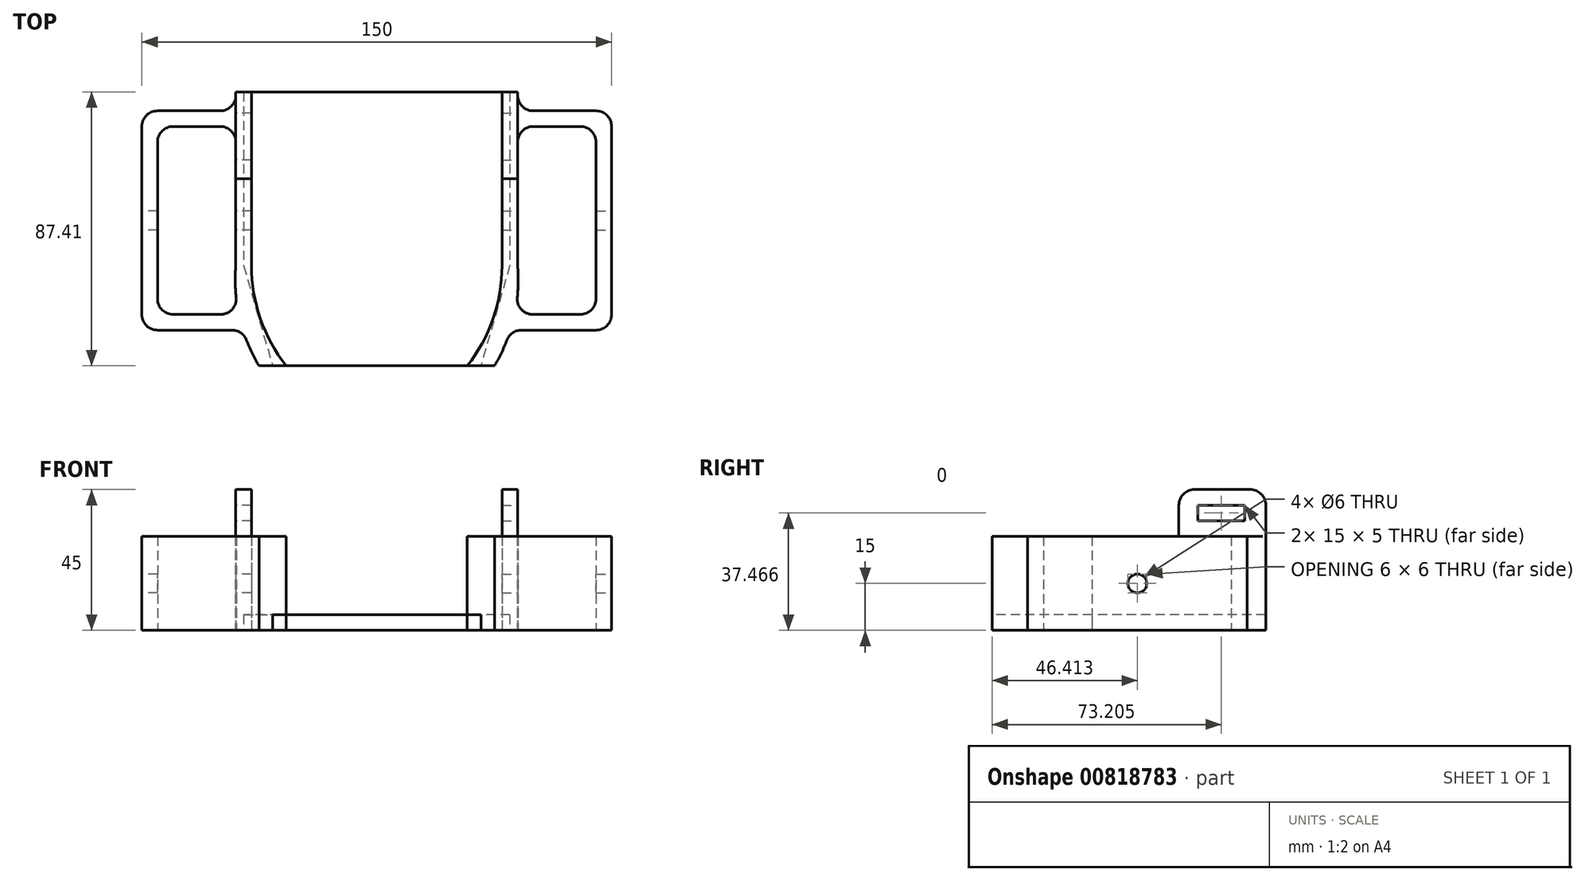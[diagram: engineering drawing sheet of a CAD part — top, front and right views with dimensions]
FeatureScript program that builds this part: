
annotation { "Feature Type Name" : "Feature", "Feature Type Description" : "" }
export const myFeature = defineFeature(function(context is Context, id is Id, definition is map)
    precondition{}
    {
        {
            var Q0;
            Q0=qCreatedBy(makeId("Top.planeOp"),FACE);
            var sketch = newSketch(context, id + "F0", { "sketchPlane" : qUnion([Q0])});
            skArc(sketch, "E0", {"start": v(-45, 0) * mm, "mid": v(-43.78, -16.56) * mm, "end": v(-37.6, -31.97) * mm});
            skLineSegment(sketch, "E1", {"start": v(-45, 0) * mm, "end": v(-45, 55.44) * mm});
            skLineSegment(sketch, "E2", {"start": v(-45, 49.44) * mm, "end": v(-75, 49.44) * mm});
            skLineSegment(sketch, "E3", {"start": v(-75, 49.44) * mm, "end": v(-75, -20.56) * mm});
            skLineSegment(sketch, "E4", {"start": v(-75, -20.56) * mm, "end": v(-42.7, -20.56) * mm});
            skLineSegment(sketch, "E5", {"start": v(-45, 44.44) * mm, "end": v(-70, 44.44) * mm});
            skLineSegment(sketch, "E6", {"start": v(-70, 44.44) * mm, "end": v(-70, -15.56) * mm});
            skLineSegment(sketch, "E7", {"start": v(-70, -15.56) * mm, "end": v(-44, -15.56) * mm});
            skLineSegment(sketch, "E8.MirrorCS", {"start": v(45, 0) * mm, "end": v(45, 55.44) * mm});
            skArc(sketch, "E9.MirrorCS", {"start": v(45, 0) * mm, "mid": v(43.78, -16.56) * mm, "end": v(37.6, -31.97) * mm});
            skLineSegment(sketch, "E10.MirrorCS", {"start": v(70, -15.56) * mm, "end": v(44, -15.56) * mm});
            skLineSegment(sketch, "E11.MirrorCS", {"start": v(75, -20.56) * mm, "end": v(42.7, -20.56) * mm});
            skLineSegment(sketch, "E12.MirrorCS", {"start": v(75, 49.44) * mm, "end": v(75, -20.56) * mm});
            skLineSegment(sketch, "E13.MirrorCS", {"start": v(70, 44.44) * mm, "end": v(70, -15.56) * mm});
            skLineSegment(sketch, "E14.MirrorCS", {"start": v(45, 44.44) * mm, "end": v(70, 44.44) * mm});
            skLineSegment(sketch, "E15.MirrorCS", {"start": v(45, 49.44) * mm, "end": v(75, 49.44) * mm});
            skLineSegment(sketch, "E16", {"start": v(-40, 55.44) * mm, "end": v(-40, 0) * mm});
            skArc(sketch, "E17", {"start": v(-40, 0) * mm, "mid": v(-37.14, -16.92) * mm, "end": v(-28.89, -31.97) * mm});
            skLineSegment(sketch, "E18.MirrorCS", {"start": v(40, 55.44) * mm, "end": v(40, 0) * mm});
            skArc(sketch, "E19.MirrorCS", {"start": v(40, 0) * mm, "mid": v(37.14, -16.92) * mm, "end": v(28.89, -31.97) * mm});
            skLineSegment(sketch, "E20", {"start": v(-45, 55.44) * mm, "end": v(-40, 55.44) * mm});
            skLineSegment(sketch, "E21.MirrorCS", {"start": v(45, 55.44) * mm, "end": v(40, 55.44) * mm});
            skLineSegment(sketch, "E22", {"start": v(-37.6, -31.97) * mm, "end": v(-28.89, -31.97) * mm});
            skPoint(sketch, "E23.orphan", {"position": v(0, -57.67) * mm});
            skLineSegment(sketch, "E24.trimOffspring", {"start": v(28.89, -31.97) * mm, "end": v(37.6, -31.97) * mm});
            skPoint(sketch, "E25.orphan", {"position": v(0, -50.23) * mm});
            skSolve(sketch);
        }
        {
            var Q0;
            Q0=qSketchRegion(id+"F0",true);
            extrude(context, id + "F1", {"entities" : qUnion([Q0]), "depth" : 30 * mm, "offsetDistance" : 25 * mm});
        }
        {
            var Q0;
            Q0=makeQuery(id+"F1.opExtrude","CAP_FACE",FACE,{"disambiguationData":[OSD([sQuery(id+"F0.wireOp",EDGE,"E0"),sQuery(id+"F0.wireOp",EDGE,"E1"),sQuery(id+"F0.wireOp",EDGE,"E2"),sQuery(id+"F0.wireOp",EDGE,"E3"),sQuery(id+"F0.wireOp",EDGE,"E4"),sQuery(id+"F0.wireOp",EDGE,"E5"),sQuery(id+"F0.wireOp",EDGE,"E6"),sQuery(id+"F0.wireOp",EDGE,"E7"),sQuery(id+"F0.wireOp",EDGE,"E16"),sQuery(id+"F0.wireOp",EDGE,"E17"),sQuery(id+"F0.wireOp",EDGE,"E20"),sQuery(id+"F0.wireOp",EDGE,"E22")])],"isStart":true});
            var sketch = newSketch(context, id + "F2", { "sketchPlane" : qUnion([Q0])});
            skLineSegment(sketch, "E26", {"start": v(-42.5, -55.44) * mm, "end": v(0, -55.44) * mm});
            skLineSegment(sketch, "E27", {"start": v(0, -55.44) * mm, "end": v(0, 31.97) * mm});
            skLineSegment(sketch, "E28", {"start": v(0, 31.97) * mm, "end": v(-33.24, 31.97) * mm});
            skLineSegment(sketch, "E29.MirrorCS", {"start": v(42.5, -55.44) * mm, "end": v(0, -55.44) * mm});
            skLineSegment(sketch, "E30.MirrorCS", {"start": v(0, 31.97) * mm, "end": v(33.24, 31.97) * mm});
            skLineSegment(sketch, "E31", {"start": v(-42.5, -55.44) * mm, "end": v(-42.5, 0) * mm});
            skLineSegment(sketch, "E32", {"start": v(-42.5, 0) * mm, "end": v(-33.24, 31.97) * mm});
            skLineSegment(sketch, "E33.MirrorCS", {"start": v(42.5, -55.44) * mm, "end": v(42.5, 0) * mm});
            skLineSegment(sketch, "E34.MirrorCS", {"start": v(42.5, 0) * mm, "end": v(33.24, 31.97) * mm});
            skSolve(sketch);
        }
        {
            var Q0;
            Q0=qSketchRegion(id+"F2",true);
            extrude(context, id + "F3", {"entities" : qUnion([Q0]), "oppositeDirection" : true, "depth" : 5 * mm, "offsetDistance" : 25 * mm});
        }
        {
            var Q0;
            Q0=makeQuery(id+"F1.opExtrude","SWEPT_FACE",FACE,{"disambiguationData":[OSD([sQuery(id+"F0.wireOp",EDGE,"E12.MirrorCS")])]});
            var sketch = newSketch(context, id + "F4", { "sketchPlane" : qUnion([Q0])});
            skCircle(sketch, "E35", {"center": v(14.44, 15) * mm, "radius": 3 * mm});
            skSolve(sketch);
        }
        {
            var Q0;
            Q0=qSketchRegion(id+"F4",true);
            extrude(context, id + "F5", {"entities" : qUnion([Q0]), "operationType" : NewBodyOperationType.REMOVE, "oppositeDirection" : true, "depth" : 35 * mm, "offsetDistance" : 25 * mm});
        }
        {
            var Q0;
            Q0=makeQuery(id+"F1.opExtrude","SWEPT_FACE",FACE,{"disambiguationData":[OSD([sQuery(id+"F0.wireOp",EDGE,"E3")])]});
            var sketch = newSketch(context, id + "F6", { "sketchPlane" : qUnion([Q0])});
            skCircle(sketch, "E36", {"center": v(-14.44, 15) * mm, "radius": 3 * mm});
            skSolve(sketch);
        }
        {
            var Q0;
            Q0=qSketchRegion(id+"F6",true);
            extrude(context, id + "F7", {"entities" : qUnion([Q0]), "operationType" : NewBodyOperationType.REMOVE, "oppositeDirection" : true, "depth" : 35 * mm, "offsetDistance" : 25 * mm});
        }
        {
            var Q0;
            Q0=makeQuery(id+"F1.opExtrude","SWEPT_FACE",FACE,{"disambiguationData":[OSD([sQuery(id+"F0.wireOp",EDGE,"E18.MirrorCS")])]});
            var sketch = newSketch(context, id + "F8", { "sketchPlane" : qUnion([Q0])});
            skPoint(sketch, "E37.oppositeSnap0", {"position": v(-27.72, 30) * mm});
            skLineSegment(sketch, "E37.bottom", {"start": v(-55.44, 30) * mm, "end": v(-27.72, 30) * mm});
            skLineSegment(sketch, "E37.top", {"start": v(-55.44, 45) * mm, "end": v(-27.72, 45) * mm});
            skLineSegment(sketch, "E37.left", {"start": v(-55.44, 30) * mm, "end": v(-55.44, 45) * mm});
            skLineSegment(sketch, "E37.right", {"start": v(-27.72, 30) * mm, "end": v(-27.72, 45) * mm});
            skLineSegment(sketch, "E38.bottom", {"start": v(-48.74, 39.97) * mm, "end": v(-33.74, 39.97) * mm});
            skLineSegment(sketch, "E38.top", {"start": v(-48.74, 34.97) * mm, "end": v(-33.74, 34.97) * mm});
            skLineSegment(sketch, "E38.left", {"start": v(-48.74, 39.97) * mm, "end": v(-48.74, 34.97) * mm});
            skLineSegment(sketch, "E38.right", {"start": v(-33.74, 39.97) * mm, "end": v(-33.74, 34.97) * mm});
            skSolve(sketch);
        }
        {
            var Q0;
            {var subQ0=sQuery(id+"F0.wireOp",EDGE,"E1");Q0=makeQuery(id+"F1.opExtrude","SWEPT_FACE",FACE,{"disambiguationData":[OSD([subQ0]),TDD([makeQuery(id+"F0.imprint","IMPRINT",EDGE,{"disambiguationData":[TD([[makeQuery(id+"F0.imprint","INTERSECT",VERTEX,{"derivedFrom":[subQ0,sQuery(id+"F0.wireOp",EDGE,"E20")]}),1.0]])],"derivedFrom":subQ0})])]});}
            var sketch = newSketch(context, id + "F9", { "sketchPlane" : qUnion([Q0])});
            skLineSegment(sketch, "E39.bottom", {"start": v(-55.44, 45) * mm, "end": v(-27.72, 45) * mm});
            skLineSegment(sketch, "E39.top", {"start": v(-55.44, 30) * mm, "end": v(-27.72, 30) * mm});
            skLineSegment(sketch, "E39.left", {"start": v(-55.44, 45) * mm, "end": v(-55.44, 30) * mm});
            skLineSegment(sketch, "E39.right", {"start": v(-27.72, 45) * mm, "end": v(-27.72, 30) * mm});
            skLineSegment(sketch, "E40.bottom", {"start": v(-48.74, 39.97) * mm, "end": v(-33.74, 39.97) * mm});
            skLineSegment(sketch, "E40.top", {"start": v(-48.74, 34.97) * mm, "end": v(-33.74, 34.97) * mm});
            skLineSegment(sketch, "E40.left", {"start": v(-48.74, 39.97) * mm, "end": v(-48.74, 34.97) * mm});
            skLineSegment(sketch, "E40.right", {"start": v(-33.74, 39.97) * mm, "end": v(-33.74, 34.97) * mm});
            skSolve(sketch);
        }
        {
            var Q0;
            Q0=qSketchRegion(id+"F9",true);
            extrude(context, id + "F10", {"entities" : qUnion([Q0]), "operationType" : NewBodyOperationType.ADD, "oppositeDirection" : true, "depth" : 5 * mm, "offsetDistance" : 25 * mm});
        }
        {
            var Q0;
            Q0=makeQuery(id+"F1.opExtrude","SWEPT_EDGE",EDGE,{"disambiguationData":[OSD([sQuery(id+"F0.wireOp",EDGE,"E2"),sQuery(id+"F0.wireOp",EDGE,"E3")])]});
            var Q1;
            Q1=makeQuery(id+"F1.opExtrude","SWEPT_EDGE",EDGE,{"disambiguationData":[OSD([sQuery(id+"F0.wireOp",EDGE,"E3"),sQuery(id+"F0.wireOp",EDGE,"E4")])]});
            fillet(context, id + "F11", {"entities" : qUnion([Q0, Q1]), "radius" : 5 * mm, "tangentPropagation" : true, "allowEdgeOverflow" : false});
        }
        {
            var Q0;
            Q0=makeQuery(id+"F1.opExtrude","SWEPT_EDGE",EDGE,{"disambiguationData":[OSD([sQuery(id+"F0.wireOp",EDGE,"E11.MirrorCS"),sQuery(id+"F0.wireOp",EDGE,"E12.MirrorCS")])]});
            var Q1;
            Q1=makeQuery(id+"F1.opExtrude","SWEPT_EDGE",EDGE,{"disambiguationData":[OSD([sQuery(id+"F0.wireOp",EDGE,"E12.MirrorCS"),sQuery(id+"F0.wireOp",EDGE,"E15.MirrorCS")])]});
            fillet(context, id + "F12", {"entities" : qUnion([Q0, Q1]), "radius" : 5 * mm, "tangentPropagation" : true, "allowEdgeOverflow" : false});
        }
        {
            var Q0;
            Q0=makeQuery(id+"F1.opExtrude","SWEPT_EDGE",EDGE,{"disambiguationData":[OSD([sQuery(id+"F0.wireOp",EDGE,"E13.MirrorCS"),sQuery(id+"F0.wireOp",EDGE,"E14.MirrorCS")])]});
            var Q1;
            Q1=makeQuery(id+"F1.opExtrude","SWEPT_EDGE",EDGE,{"disambiguationData":[OSD([sQuery(id+"F0.wireOp",EDGE,"E10.MirrorCS"),sQuery(id+"F0.wireOp",EDGE,"E13.MirrorCS")])]});
            var Q2;
            Q2=makeQuery(id+"F1.opExtrude","SWEPT_EDGE",EDGE,{"disambiguationData":[OSD([sQuery(id+"F0.wireOp",EDGE,"E5"),sQuery(id+"F0.wireOp",EDGE,"E6")])]});
            var Q3;
            Q3=makeQuery(id+"F1.opExtrude","SWEPT_EDGE",EDGE,{"disambiguationData":[OSD([sQuery(id+"F0.wireOp",EDGE,"E6"),sQuery(id+"F0.wireOp",EDGE,"E7")])]});
            var Q4;
            Q4=makeQuery(id+"F1.opExtrude","SWEPT_EDGE",EDGE,{"disambiguationData":[OSD([sQuery(id+"F0.wireOp",EDGE,"E1"),sQuery(id+"F0.wireOp",EDGE,"E5")])]});
            var Q5;
            Q5=makeQuery(id+"F1.opExtrude","SWEPT_EDGE",EDGE,{"disambiguationData":[OSD([sQuery(id+"F0.wireOp",EDGE,"E8.MirrorCS"),sQuery(id+"F0.wireOp",EDGE,"E14.MirrorCS")])]});
            var Q6;
            Q6=makeQuery(id+"F1.opExtrude","SWEPT_EDGE",EDGE,{"disambiguationData":[OSD([sQuery(id+"F0.wireOp",EDGE,"E9.MirrorCS"),sQuery(id+"F0.wireOp",EDGE,"E10.MirrorCS")])]});
            var Q7;
            Q7=makeQuery(id+"F1.opExtrude","SWEPT_EDGE",EDGE,{"disambiguationData":[OSD([sQuery(id+"F0.wireOp",EDGE,"E0"),sQuery(id+"F0.wireOp",EDGE,"E7")])]});
            var Q8;
            Q8=makeQuery(id+"F1.opExtrude","SWEPT_EDGE",EDGE,{"disambiguationData":[OSD([sQuery(id+"F0.wireOp",EDGE,"E9.MirrorCS"),sQuery(id+"F0.wireOp",EDGE,"E11.MirrorCS")])]});
            var Q9;
            Q9=makeQuery(id+"F1.opExtrude","SWEPT_EDGE",EDGE,{"disambiguationData":[OSD([sQuery(id+"F0.wireOp",EDGE,"E0"),sQuery(id+"F0.wireOp",EDGE,"E4")])]});
            var Q10;
            Q10=makeQuery(id+"F1.opExtrude","SWEPT_EDGE",EDGE,{"disambiguationData":[OSD([sQuery(id+"F0.wireOp",EDGE,"E8.MirrorCS"),sQuery(id+"F0.wireOp",EDGE,"E15.MirrorCS")])]});
            var Q11;
            Q11=makeQuery(id+"F1.opExtrude","SWEPT_EDGE",EDGE,{"disambiguationData":[OSD([sQuery(id+"F0.wireOp",EDGE,"E1"),sQuery(id+"F0.wireOp",EDGE,"E2")])]});
            var Q12;
            Q12=makeQuery(id+"F10.opExtrude","SWEPT_EDGE",EDGE,{"disambiguationData":[OSD([sQuery(id+"F9.wireOp",EDGE,"E39.top"),sQuery(id+"F9.wireOp",EDGE,"E39.right")])]});
            fillet(context, id + "F13", {"entities" : qUnion([Q0, Q1, Q2, Q3, Q4, Q5, Q6, Q7, Q8, Q9, Q10, Q11, Q12]), "radius" : 5 * mm, "tangentPropagation" : true, "allowEdgeOverflow" : false});
        }
        {
            var Q0;
            Q0=makeQuery(id+"F10.opExtrude","SWEPT_EDGE",EDGE,{"disambiguationData":[OSD([sQuery(id+"F9.wireOp",EDGE,"E39.bottom"),sQuery(id+"F9.wireOp",EDGE,"E39.left")])]});
            var Q1;
            Q1=makeQuery(id+"FJua1TxrDA2uPtG_3.opExtrude","SWEPT_EDGE",EDGE,{"disambiguationData":[OSD([sQuery(id+"F8.wireOp",EDGE,"E37.top"),sQuery(id+"F8.wireOp",EDGE,"E37.left")])]});
            var Q2;
            Q2=makeQuery(id+"FJua1TxrDA2uPtG_3.opExtrude","SWEPT_EDGE",EDGE,{"disambiguationData":[OSD([sQuery(id+"F8.wireOp",EDGE,"E37.top"),sQuery(id+"F8.wireOp",EDGE,"E37.right")])]});
            var Q3;
            Q3=makeQuery(id+"F10.opExtrude","SWEPT_EDGE",EDGE,{"disambiguationData":[OSD([sQuery(id+"F9.wireOp",EDGE,"E39.bottom"),sQuery(id+"F9.wireOp",EDGE,"E39.right")])]});
            fillet(context, id + "F14", {"entities" : qUnion([Q0, Q1, Q2, Q3]), "radius" : 5 * mm, "tangentPropagation" : true, "allowEdgeOverflow" : false});
        }
        {
            var Q0;
            {var subQ0=sQuery(id+"F0.wireOp",EDGE,"E8.MirrorCS");Q0=makeQuery(id+"F1.opExtrude","SWEPT_FACE",FACE,{"disambiguationData":[OSD([subQ0]),TDD([makeQuery(id+"F0.imprint","IMPRINT",EDGE,{"disambiguationData":[TD([[makeQuery(id+"F0.imprint","INTERSECT",VERTEX,{"derivedFrom":[subQ0,sQuery(id+"F0.wireOp",EDGE,"E9.MirrorCS")]}),-1.0]])],"derivedFrom":subQ0})])]});}
            var sketch = newSketch(context, id + "F15", { "sketchPlane" : qUnion([Q0])});
            skLineSegment(sketch, "E41.bottom", {"start": v(27.72, 45) * mm, "end": v(55.44, 45) * mm});
            skLineSegment(sketch, "E41.top", {"start": v(27.72, 30) * mm, "end": v(55.44, 30) * mm});
            skLineSegment(sketch, "E41.left", {"start": v(27.72, 45) * mm, "end": v(27.72, 30) * mm});
            skLineSegment(sketch, "E41.right", {"start": v(55.44, 45) * mm, "end": v(55.44, 30) * mm});
            skLineSegment(sketch, "E42.bottom", {"start": v(33.74, 39.97) * mm, "end": v(48.74, 39.97) * mm});
            skLineSegment(sketch, "E42.top", {"start": v(33.74, 34.97) * mm, "end": v(48.74, 34.97) * mm});
            skLineSegment(sketch, "E42.left", {"start": v(33.74, 39.97) * mm, "end": v(33.74, 34.97) * mm});
            skLineSegment(sketch, "E42.right", {"start": v(48.74, 39.97) * mm, "end": v(48.74, 34.97) * mm});
            skSolve(sketch);
        }
        {
            var Q0;
            Q0=qSketchRegion(id+"F15",true);
            extrude(context, id + "F16", {"entities" : qUnion([Q0]), "operationType" : NewBodyOperationType.ADD, "oppositeDirection" : true, "depth" : 5 * mm, "offsetDistance" : 25 * mm});
        }
        {
            var Q0;
            Q0=makeQuery(id+"F16.opExtrude","SWEPT_EDGE",EDGE,{"disambiguationData":[OSD([sQuery(id+"F15.wireOp",EDGE,"E41.bottom"),sQuery(id+"F15.wireOp",EDGE,"E41.right")])]});
            var Q1;
            Q1=makeQuery(id+"F16.opExtrude","SWEPT_EDGE",EDGE,{"disambiguationData":[OSD([sQuery(id+"F15.wireOp",EDGE,"E41.bottom"),sQuery(id+"F15.wireOp",EDGE,"E41.left")])]});
            var Q2;
            Q2=makeQuery(id+"F16.opExtrude","SWEPT_EDGE",EDGE,{"disambiguationData":[OSD([sQuery(id+"F0.wireOp",EDGE,"E8.MirrorCS"),sQuery(id+"F15.wireOp",EDGE,"E41.top"),sQuery(id+"F15.wireOp",EDGE,"E41.left")])]});
            fillet(context, id + "F17", {"entities" : qUnion([Q0, Q1, Q2]), "radius" : 5 * mm, "tangentPropagation" : true, "allowEdgeOverflow" : false});
        }
    });
